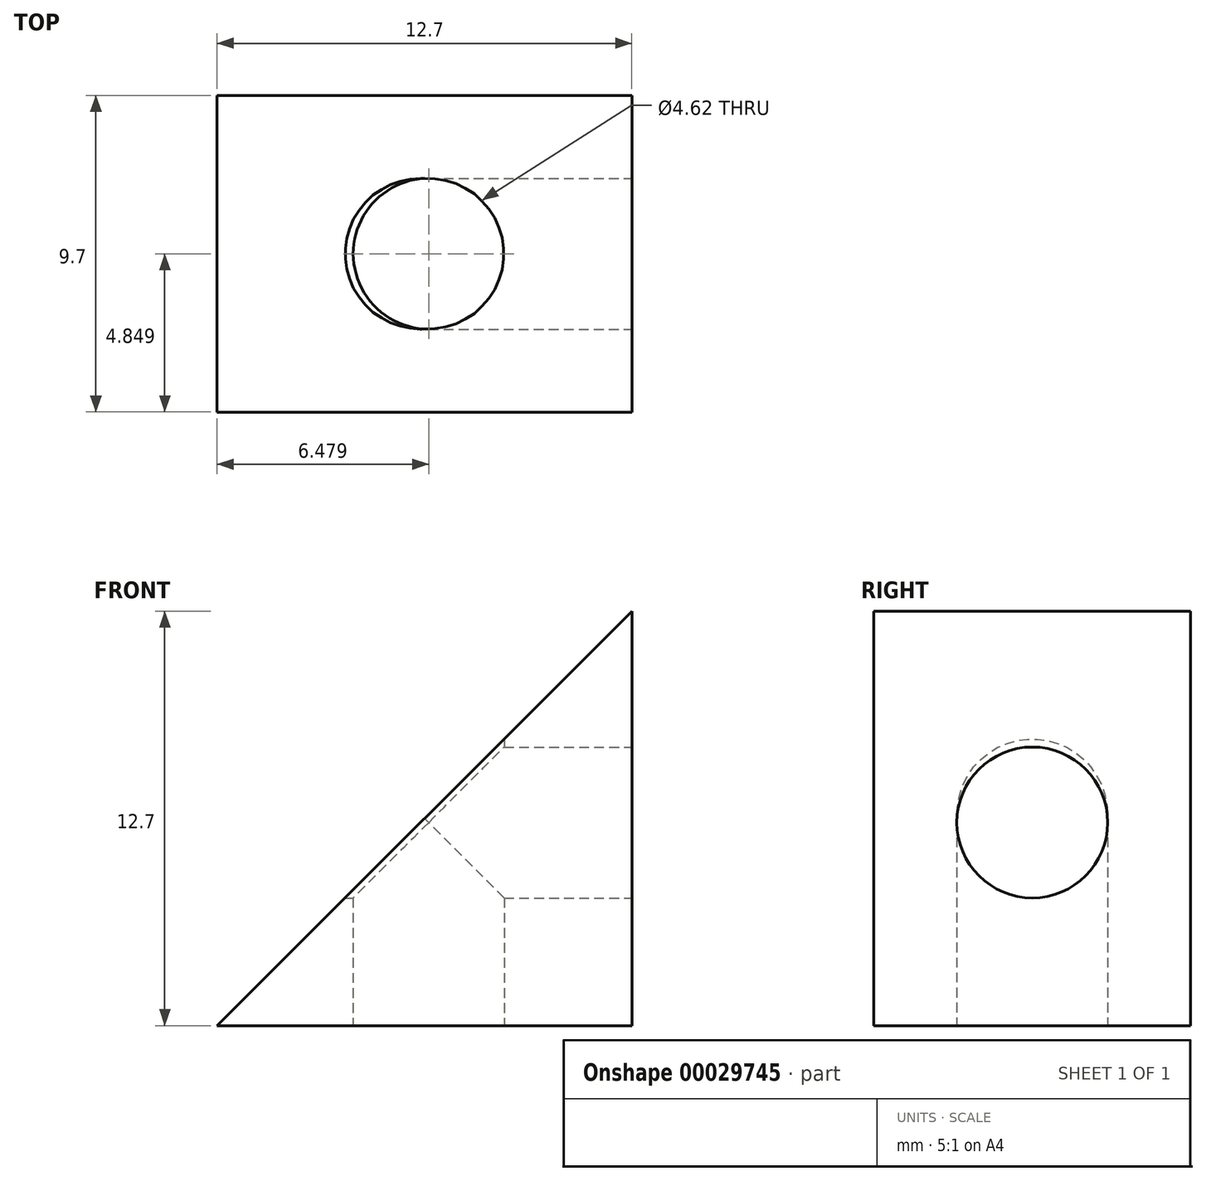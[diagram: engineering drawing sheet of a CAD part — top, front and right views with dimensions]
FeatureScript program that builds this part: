
annotation { "Feature Type Name" : "Feature", "Feature Type Description" : "" }
export const myFeature = defineFeature(function(context is Context, id is Id, definition is map)
    precondition{}
    {
        {
            var Q0;
            Q0=qCreatedBy(makeId("Front.planeOp"),FACE);
            var sketch = newSketch(context, id + "F0", { "sketchPlane" : qUnion([Q0])});
            skLineSegment(sketch, "E0", {"start": v(-3.8, 16.4) * mm, "end": v(-3.8, 3.7) * mm});
            skLineSegment(sketch, "E1", {"start": v(-3.8, 3.7) * mm, "end": v(-16.5, 3.7) * mm});
            skLineSegment(sketch, "E2", {"start": v(-16.5, 3.7) * mm, "end": v(-3.8, 16.4) * mm});
            skSolve(sketch);
        }
        {
            var Q0;
            Q0=makeQuery(id+"F0.imprint","IMPRINT",FACE,{"disambiguationData":[TD([[makeQuery(id+"F0.imprint","IMPRINT",EDGE,{"derivedFrom":sQuery(id+"F0.wireOp",EDGE,"E0")}),-1.0]])]});
            extrude(context, id + "F1", {"entities" : qUnion([Q0]), "depth" : 9.7 * mm});
        }
        {
            var Q0;
            Q0=makeQuery(id+"F1.opExtrude","SWEPT_FACE",FACE,{"disambiguationData":[OSD([sQuery(id+"F0.wireOp",EDGE,"E0")])]});
            var sketch = newSketch(context, id + "F2", { "sketchPlane" : qUnion([Q0])});
            skCircle(sketch, "E3", {"center": v(-4.85, 9.92) * mm, "radius": 2.31 * mm});
            skPoint(sketch, "E4.endSnap0", {"position": v(-9.7, 10.05) * mm});
            skSolve(sketch);
        }
        {
            var Q0;
            Q0=makeQuery(id+"F1.opExtrude","SWEPT_FACE",FACE,{"disambiguationData":[OSD([sQuery(id+"F0.wireOp",EDGE,"E1")])]});
            var sketch = newSketch(context, id + "F3", { "sketchPlane" : qUnion([Q0])});
            skLineSegment(sketch, "E5", {"start": v(-3.8, 4.85) * mm, "end": v(-7.7, 4.85) * mm});
            skPoint(sketch, "E5.endSnap0", {"position": v(-3.8, 4.85) * mm});
            skCircle(sketch, "E6", {"center": v(-10.02, 4.85) * mm, "radius": 2.31 * mm});
            skSolve(sketch);
        }
        {
            var Q0;
            Q0=makeQuery(id+"F2.imprint","IMPRINT",FACE,{"disambiguationData":[TD([[makeQuery(id+"F2.imprint","IMPRINT",EDGE,{"derivedFrom":sQuery(id+"F2.wireOp",EDGE,"E3")}),1.0]])]});
            extrude(context, id + "F4", {"entities" : qUnion([Q0]), "operationType" : NewBodyOperationType.REMOVE, "oppositeDirection" : true, "depth" : 8.9 * mm});
        }
        {
            var Q0;
            Q0=makeQuery(id+"F3.imprint","IMPRINT",FACE,{"disambiguationData":[TD([[makeQuery(id+"F3.imprint","IMPRINT",EDGE,{"derivedFrom":sQuery(id+"F3.wireOp",EDGE,"E6")}),1.0]])]});
            extrude(context, id + "F5", {"entities" : qUnion([Q0]), "operationType" : NewBodyOperationType.REMOVE, "oppositeDirection" : true, "depth" : 8.9 * mm});
        }
    });
